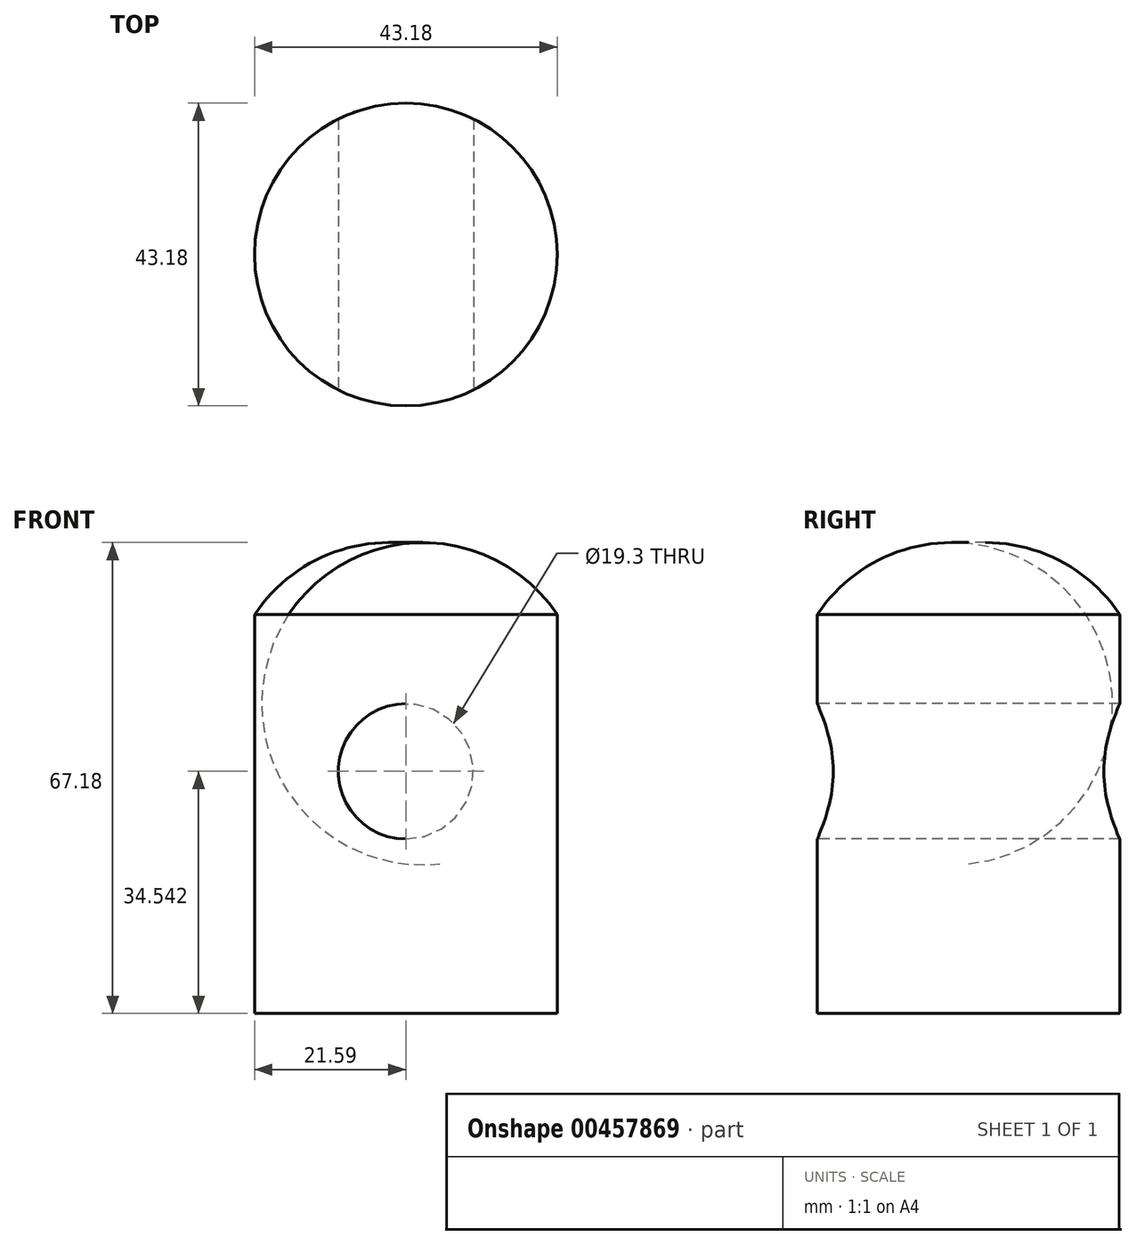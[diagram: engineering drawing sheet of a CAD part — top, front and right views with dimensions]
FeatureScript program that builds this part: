
annotation { "Feature Type Name" : "Feature", "Feature Type Description" : "" }
export const myFeature = defineFeature(function(context is Context, id is Id, definition is map)
    precondition{}
    {
        {
            var Q0;
            Q0=qCreatedBy(makeId("Front.planeOp"),FACE);
            var sketch = newSketch(context, id + "F0", { "sketchPlane" : qUnion([Q0])});
            skLineSegment(sketch, "E0", {"start": v(0, -24.9) * mm, "end": v(-21.6, -24.9) * mm});
            skLineSegment(sketch, "E1", {"start": v(-21.59, -24.9) * mm, "end": v(-21.59, 32) * mm});
            skLineSegment(sketch, "E2", {"start": v(0, -24.9) * mm, "end": v(0, 0) * mm});
            skArc(sketch, "E3", {"start": v(0, 42.16) * mm, "mid": v(-12.22, 40.1) * mm, "end": v(-21.6, 32) * mm});
            skLineSegment(sketch, "E4", {"start": v(-21.59, -24.9) * mm, "end": v(-21.59, 0) * mm});
            skLineSegment(sketch, "E5", {"start": v(-21.59, 0) * mm, "end": v(-21.59, 19.3) * mm});
            skPoint(sketch, "E6.end.orphan", {"position": v(0, 19.3) * mm});
            skPoint(sketch, "E7.center.orphan", {"position": v(0, 9.65) * mm});
            skPoint(sketch, "E8.MirrorCS.center.orphan", {"position": v(2.43, 19.3) * mm});
            skPoint(sketch, "E8.MirrorCS.end.orphan", {"position": v(21.6, 32) * mm});
            skPoint(sketch, "E8.MirrorCS.start.orphan", {"position": v(0, 42.16) * mm});
            skPoint(sketch, "E9.orphan", {"position": v(21.59, 32) * mm});
            skPoint(sketch, "E10.MirrorCS.start.orphan", {"position": v(21.59, 0) * mm});
            skPoint(sketch, "E11.orphan", {"position": v(21.59, -24.9) * mm});
            skPoint(sketch, "E12.MirrorCS.end.orphan", {"position": v(21.6, -24.9) * mm});
            skPoint(sketch, "E12.MirrorCS.start.orphan", {"position": v(0, -24.9) * mm});
            skPoint(sketch, "E13.MirrorCS.end.orphan", {"position": v(21.59, 19.3) * mm});
            skLineSegment(sketch, "E14", {"start": v(0, 42.16) * mm, "end": v(0, -24.9) * mm});
            skSolve(sketch);
        }
        {
            var Q0;
            {var subQ1=sQuery(id+"F0.wireOp",EDGE,"E0");Q0=makeQuery(id+"F0.imprint","IMPRINT",FACE,{"disambiguationData":[TD([[makeQuery(id+"F0.imprint","IMPRINT",EDGE,{"derivedFrom":subQ1}),-1.0]])]});}
            var Q1;
            Q1=sQuery(id+"F0.wireOp",EDGE,"E14");
            revolve(context, id + "F1", {"entities" : qUnion([Q0]), "axis" : qUnion([Q1]), "revolveType" : RevolveType.FULL});
        }
        {
            var Q0;
            Q0=qCreatedBy(makeId("Front.planeOp"),FACE);
            var sketch = newSketch(context, id + "F2", { "sketchPlane" : qUnion([Q0])});
            skLineSegment(sketch, "E15", {"start": v(0, 0) * mm, "end": v(0, 19.3) * mm});
            skCircle(sketch, "E16", {"center": v(0, 9.65) * mm, "radius": 9.65 * mm});
            skSolve(sketch);
        }
        {
            var Q0;
            Q0 = qSketchRegion(id + "F2", true);
            extrude(context, id + "F3", {"entities" : qUnion([Q0]), "operationType" : NewBodyOperationType.REMOVE, "oppositeDirection" : true, "depth" : 21.84 * mm});
        }
        {
            var Q0;
            Q0=qCreatedBy(makeId("Front.planeOp"),FACE);
            var sketch = newSketch(context, id + "F4", { "sketchPlane" : qUnion([Q0])});
            skCircle(sketch, "E17", {"center": v(0, 9.65) * mm, "radius": 9.65 * mm});
            skPoint(sketch, "E18.orphan", {"position": v(0, 0) * mm});
            skPoint(sketch, "E19.end.orphan", {"position": v(0, 19.3) * mm});
            skSolve(sketch);
        }
        {
            var Q0;
            Q0 = qSketchRegion(id + "F4", true);
            extrude(context, id + "F5", {"entities" : qUnion([Q0]), "operationType" : NewBodyOperationType.REMOVE, "depth" : 21.84 * mm});
        }
    });
